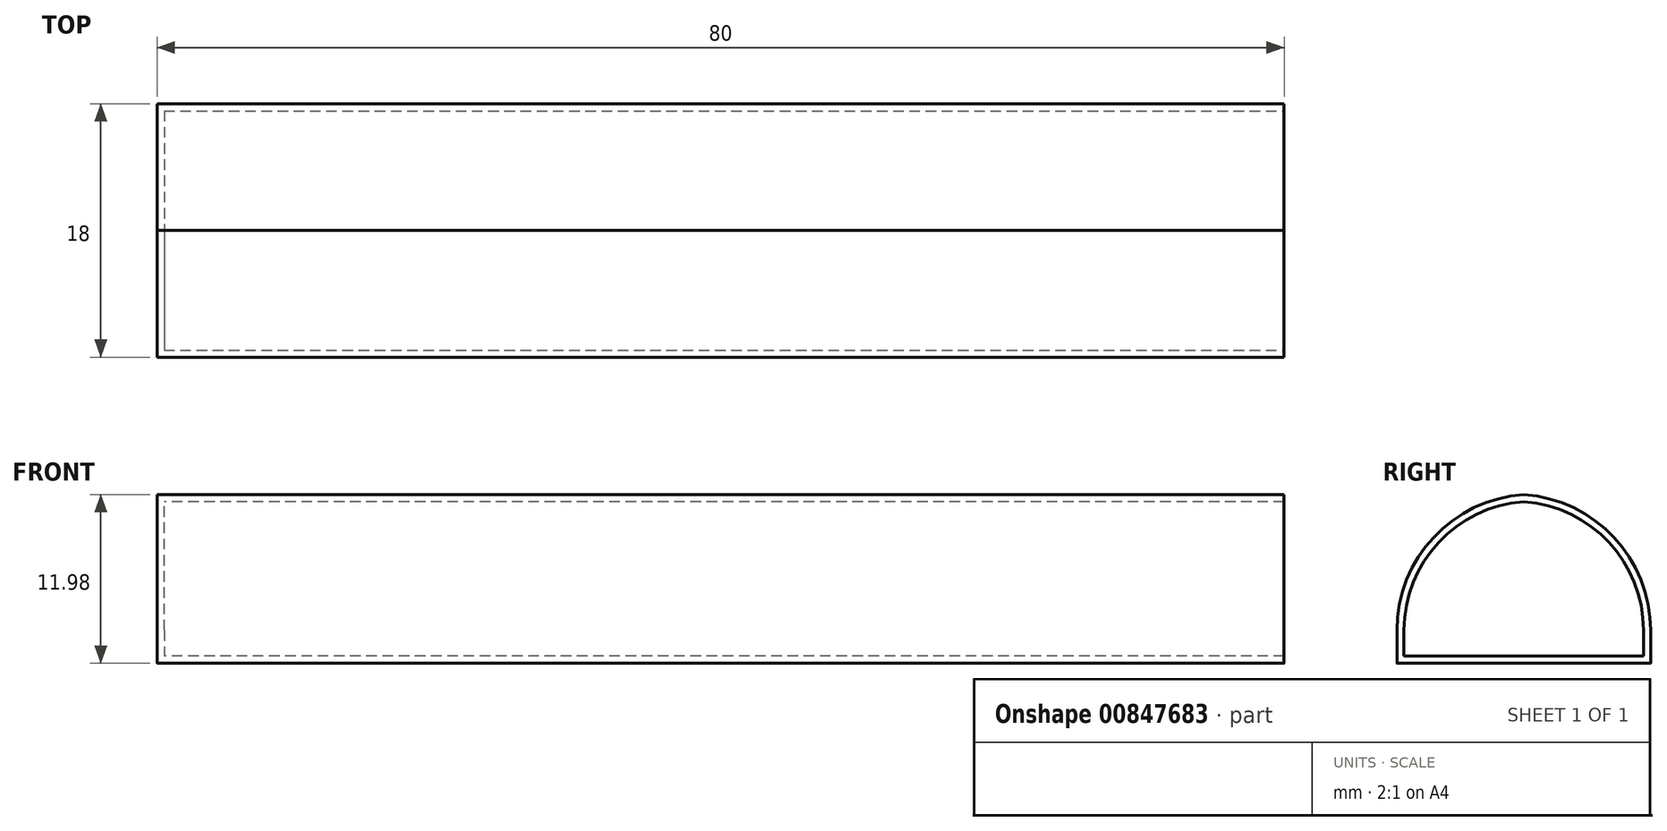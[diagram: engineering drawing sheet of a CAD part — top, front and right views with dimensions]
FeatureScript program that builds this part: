
annotation { "Feature Type Name" : "Feature", "Feature Type Description" : "" }
export const myFeature = defineFeature(function(context is Context, id is Id, definition is map)
    precondition{}
    {
        {
            var Q0;
            Q0=qCreatedBy(makeId("Top.planeOp"),FACE);
            var sketch = newSketch(context, id + "F0", { "sketchPlane" : qUnion([Q0])});
            skLineSegment(sketch, "E0.bottom", {"start": v(-145.05, -46.1) * mm, "end": v(-65.05, -46.1) * mm});
            skLineSegment(sketch, "E0.top", {"start": v(-145.05, -64.1) * mm, "end": v(-65.05, -64.1) * mm});
            skLineSegment(sketch, "E0.left", {"start": v(-145.05, -46.1) * mm, "end": v(-145.05, -64.1) * mm});
            skLineSegment(sketch, "E0.right", {"start": v(-65.05, -46.1) * mm, "end": v(-65.05, -64.1) * mm});
            skSolve(sketch);
        }
        {
            var Q0;
            Q0=makeQuery(id+"F0.imprint","IMPRINT",FACE,{"disambiguationData":[TD([[makeQuery(id+"F0.imprint","IMPRINT",EDGE,{"derivedFrom":sQuery(id+"F0.wireOp",EDGE,"E0.bottom")}),-1.0]])]});
            extrude(context, id + "F1", {"entities" : qUnion([Q0]), "depth" : 12 * mm, "offsetDistance" : 25 * mm});
        }
        {
            var Q0;
            Q0=makeQuery(id+"F1.opExtrude","CAP_EDGE",EDGE,{"disambiguationData":[OSD([sQuery(id+"F0.wireOp",EDGE,"E0.top")])],"isStart":false});
            var Q1;
            Q1=makeQuery(id+"F1.opExtrude","CAP_EDGE",EDGE,{"disambiguationData":[OSD([sQuery(id+"F0.wireOp",EDGE,"E0.bottom")])],"isStart":false});
            fillet(context, id + "F2", {"entities" : qUnion([Q0, Q1]), "radius" : 9.66 * mm, "tangentPropagation" : true, "allowEdgeOverflow" : false});
        }
        {
            var Q0;
            Q0=makeQuery(id+"F1.opExtrude","CAP_FACE",FACE,{"disambiguationData":[OSD([sQuery(id+"F0.wireOp",EDGE,"E0.bottom"),sQuery(id+"F0.wireOp",EDGE,"E0.top"),sQuery(id+"F0.wireOp",EDGE,"E0.left"),sQuery(id+"F0.wireOp",EDGE,"E0.right")])],"isStart":true});
            fillet(context, id + "F3", {"entities" : qUnion([Q0]), "radius" : 0.02 * mm, "tangentPropagation" : true, "allowEdgeOverflow" : false});
        }
        {
            var Q0;
            Q0=makeQuery(id+"F1.opExtrude","SWEPT_FACE",FACE,{"disambiguationData":[OSD([sQuery(id+"F0.wireOp",EDGE,"E0.right")])]});
            shell(context, id + "F4", {"entities" : qUnion([Q0]), "thickness" : 0.5 * mm});
        }
    });
